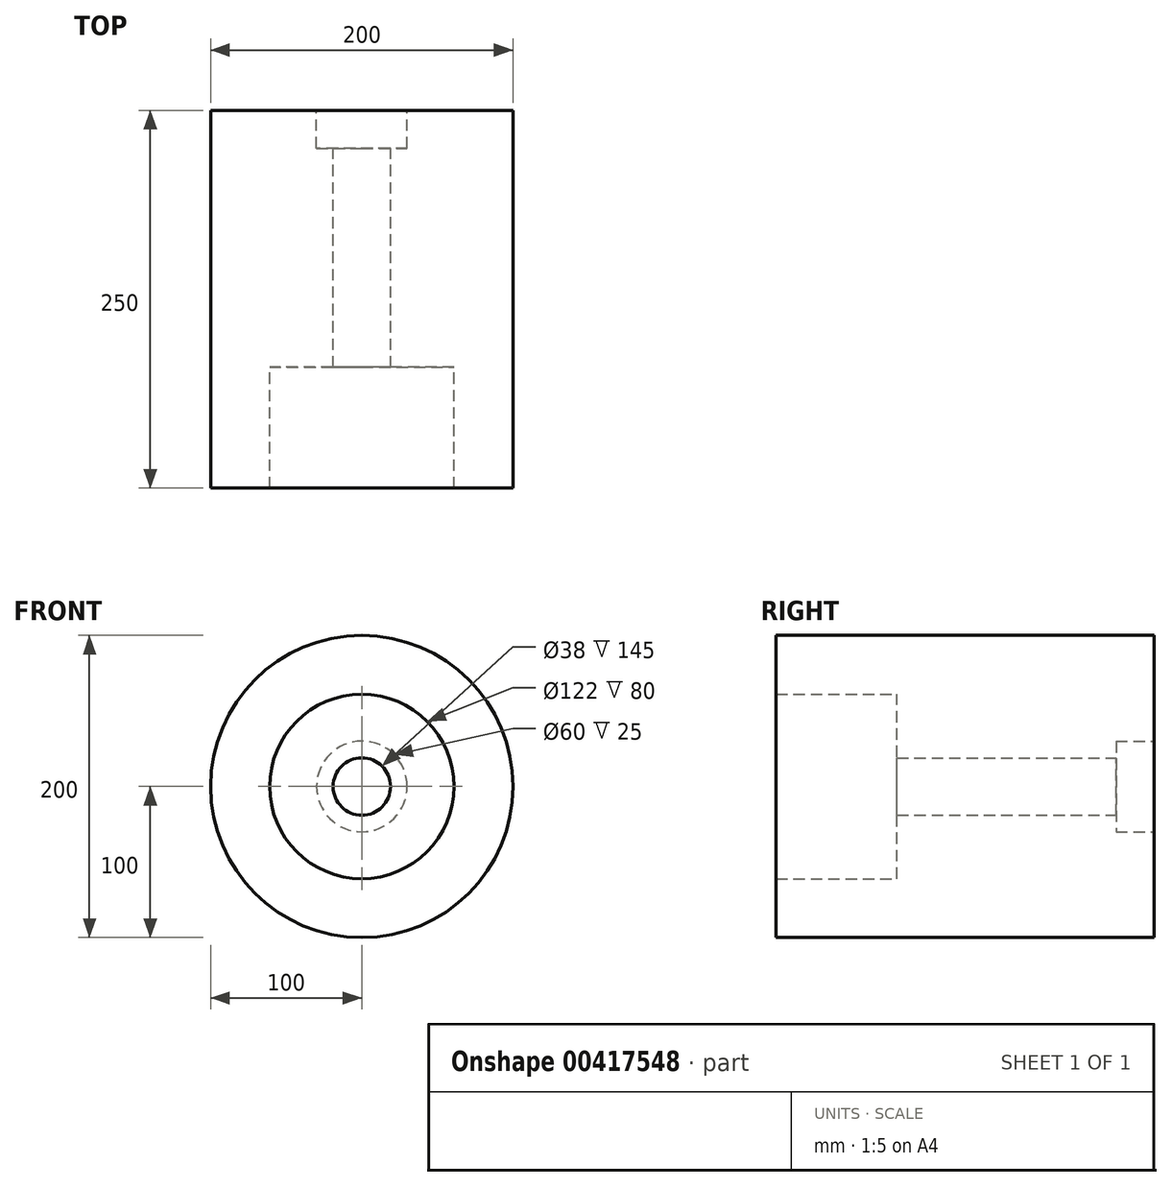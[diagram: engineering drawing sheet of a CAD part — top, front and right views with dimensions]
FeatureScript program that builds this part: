
annotation { "Feature Type Name" : "Feature", "Feature Type Description" : "" }
export const myFeature = defineFeature(function(context is Context, id is Id, definition is map)
    precondition{}
    {
        {
            var Q0;
            Q0=qCreatedBy(makeId("Front.planeOp"),FACE);
            var sketch = newSketch(context, id + "F0", { "sketchPlane" : qUnion([Q0])});
            skCircle(sketch, "E0", {"center": v(0, 0) * mm, "radius": 100 * mm});
            skCircle(sketch, "E1", {"center": v(0, 0) * mm, "radius": 19 * mm});
            skCircle(sketch, "E2", {"center": v(0, 0) * mm, "radius": 61 * mm});
            skSolve(sketch);
        }
        {
            var Q0;
            Q0=makeQuery(id+"F0.imprint","IMPRINT",FACE,{"disambiguationData":[TD([[makeQuery(id+"F0.imprint","IMPRINT",EDGE,{"derivedFrom":sQuery(id+"F0.wireOp",EDGE,"E0")}),1.0]])]});
            extrude(context, id + "F1", {"entities" : qUnion([Q0]), "depth" : 250 * mm});
        }
        {
            var Q0;
            Q0=makeQuery(id+"F0.imprint","IMPRINT",FACE,{"disambiguationData":[TD([[makeQuery(id+"F0.imprint","IMPRINT",EDGE,{"derivedFrom":sQuery(id+"F0.wireOp",EDGE,"E1")}),-1.0]])]});
            extrude(context, id + "F2", {"entities" : qUnion([Q0]), "operationType" : NewBodyOperationType.ADD, "depth" : 170 * mm});
        }
        {
            var Q0;
            {var subQ0=sQuery(id+"F0.wireOp",EDGE,"E2");Q0=makeQuery(id+"F2.boolean.opBoolean","MERGE",FACE,{"derivedFrom":[makeQuery(id+"F1.opExtrude","CAP_FACE",FACE,{"disambiguationData":[OSD([sQuery(id+"F0.wireOp",EDGE,"E0"),subQ0])],"isStart":true}),makeQuery(id+"F2.opExtrude","CAP_FACE",FACE,{"disambiguationData":[OSD([sQuery(id+"F0.wireOp",EDGE,"E1"),subQ0])],"isStart":true})]});}
            var sketch = newSketch(context, id + "F3", { "sketchPlane" : qUnion([Q0])});
            skCircle(sketch, "E3", {"center": v(0, 0) * mm, "radius": 30 * mm});
            skSolve(sketch);
        }
        {
            var Q0;
            Q0=makeQuery(id+"F3.imprint","IMPRINT",FACE,{"disambiguationData":[TD([[makeQuery(id+"F3.imprint","IMPRINT",EDGE,{"derivedFrom":sQuery(id+"F3.wireOp",EDGE,"E3")}),1.0]])]});
            extrude(context, id + "F4", {"entities" : qUnion([Q0]), "operationType" : NewBodyOperationType.REMOVE, "oppositeDirection" : true, "depth" : 25 * mm});
        }
    });
